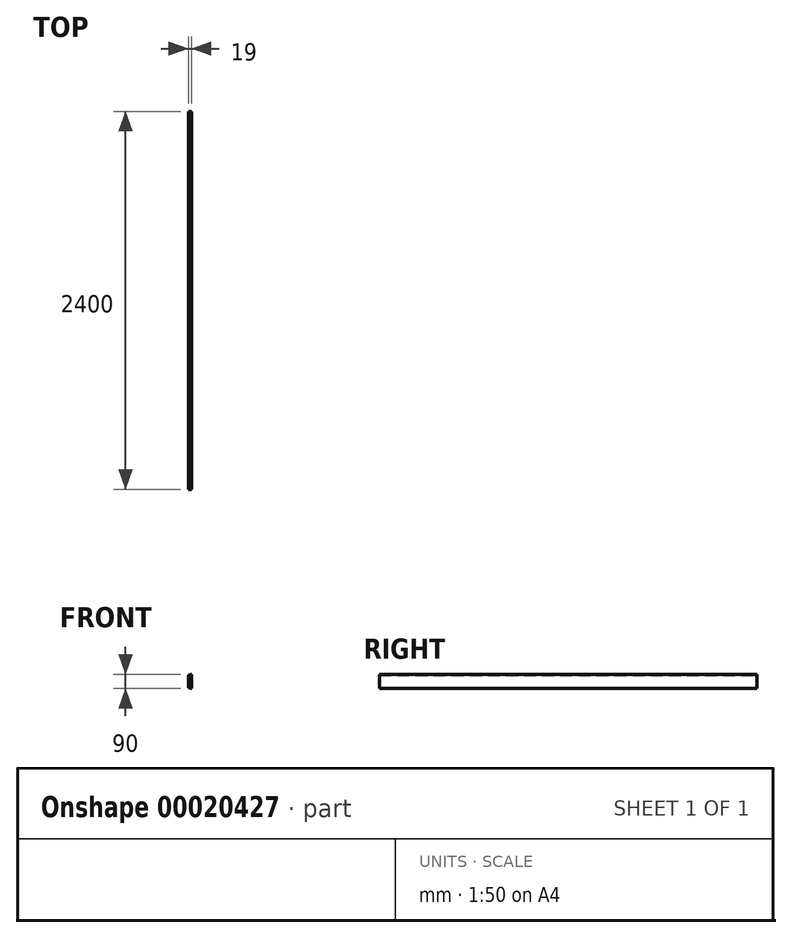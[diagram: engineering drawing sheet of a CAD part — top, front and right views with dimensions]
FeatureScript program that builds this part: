
annotation { "Feature Type Name" : "Feature", "Feature Type Description" : "" }
export const myFeature = defineFeature(function(context is Context, id is Id, definition is map)
    precondition{}
    {
        {
            var Q0;
            Q0=qCreatedBy(makeId("Front.planeOp"),FACE);
            var sketch = newSketch(context, id + "F0", { "sketchPlane" : qUnion([Q0])});
            skLineSegment(sketch, "E0", {"start": v(0, 0) * mm, "end": v(0, 90) * mm});
            skLineSegment(sketch, "E1", {"start": v(0, 90) * mm, "end": v(-6.3, 90) * mm});
            skLineSegment(sketch, "E2", {"start": v(-6.3, 90) * mm, "end": v(-6.3, 82) * mm});
            skLineSegment(sketch, "E3", {"start": v(-6.3, 82) * mm, "end": v(-12.3, 82) * mm});
            skLineSegment(sketch, "E4", {"start": v(-12.3, 82) * mm, "end": v(-12.3, 85) * mm});
            skLineSegment(sketch, "E5", {"start": v(-12.3, 85) * mm, "end": v(-19, 85) * mm});
            skLineSegment(sketch, "E6", {"start": v(-19, 85) * mm, "end": v(-19, 5) * mm});
            skLineSegment(sketch, "E7", {"start": v(-19, 5) * mm, "end": v(-12.3, 5) * mm});
            skLineSegment(sketch, "E8", {"start": v(-12.3, 5) * mm, "end": v(-12.3, 8) * mm});
            skLineSegment(sketch, "E9", {"start": v(-12.3, 8) * mm, "end": v(-6.3, 8) * mm});
            skLineSegment(sketch, "E10", {"start": v(-6.3, 8) * mm, "end": v(-6.3, 0) * mm});
            skLineSegment(sketch, "E11", {"start": v(-6.3, 0) * mm, "end": v(0, 0) * mm});
            skSolve(sketch);
        }
        {
            var Q0;
            Q0=makeQuery(id+"F0.imprint","IMPRINT",FACE,{"disambiguationData":[TD([[makeQuery(id+"F0.imprint","IMPRINT",EDGE,{"derivedFrom":sQuery(id+"F0.wireOp",EDGE,"E0")}),1.0]])]});
            extrude(context, id + "F1", {"entities" : qUnion([Q0]), "depth" : 2400 * mm});
        }
    });
